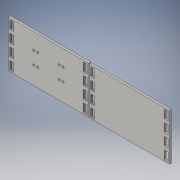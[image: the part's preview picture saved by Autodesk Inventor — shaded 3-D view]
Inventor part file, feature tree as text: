
AUTODESK INVENTOR PART (.ipt)
format: ipt  version: 2016 (Build 200138000, 138)  size: 206,336 bytes
history: native  units: in
note: dims shown in document units (in); Inventor stores cm internally (conversion verified against a paired STEP export)
features: extrude x1, sketch x1
ambient origin geometry x8: Origin, YZ Plane, XZ Plane, XY Plane, X Axis, Y Axis, Z Axis, Center Point
bodies: Body1 (feature_tree)
feature tree (2):
  extrude  "Extrusion13"  Depth=0.185in
  sketch  "Sketch1"  dims[d2=0.098in d3=0.098in d5=0.61in d7=0.098in d8=0.098in d9=0.61in d10=0.185in d19=0.185in d23=0.185in d24=0.4in d143=1.5748in d145=0.56in d146=0.3937in d148=1.0in d190=0.4in d192=0.07in d212=0.07in d215=0.07in d216=0.16in d217=0.16in d218=0.16in d219=0.4in d220=0.4in d221=0.4in d222=0.16in d223=0.07in d257=1.5748in d259=0.3937in d268=0.185in d269=0.4in d270=0.56in d271=0.4in d272=0.07in d273=0.07in d274=0.07in d275=0.16in d276=0.16in d277=0.16in d278=0.4in d279=0.4in d280=0.4in d281=0.16in d282=0.07in d283=1.0in d284=0.1in d285=0.0in]
